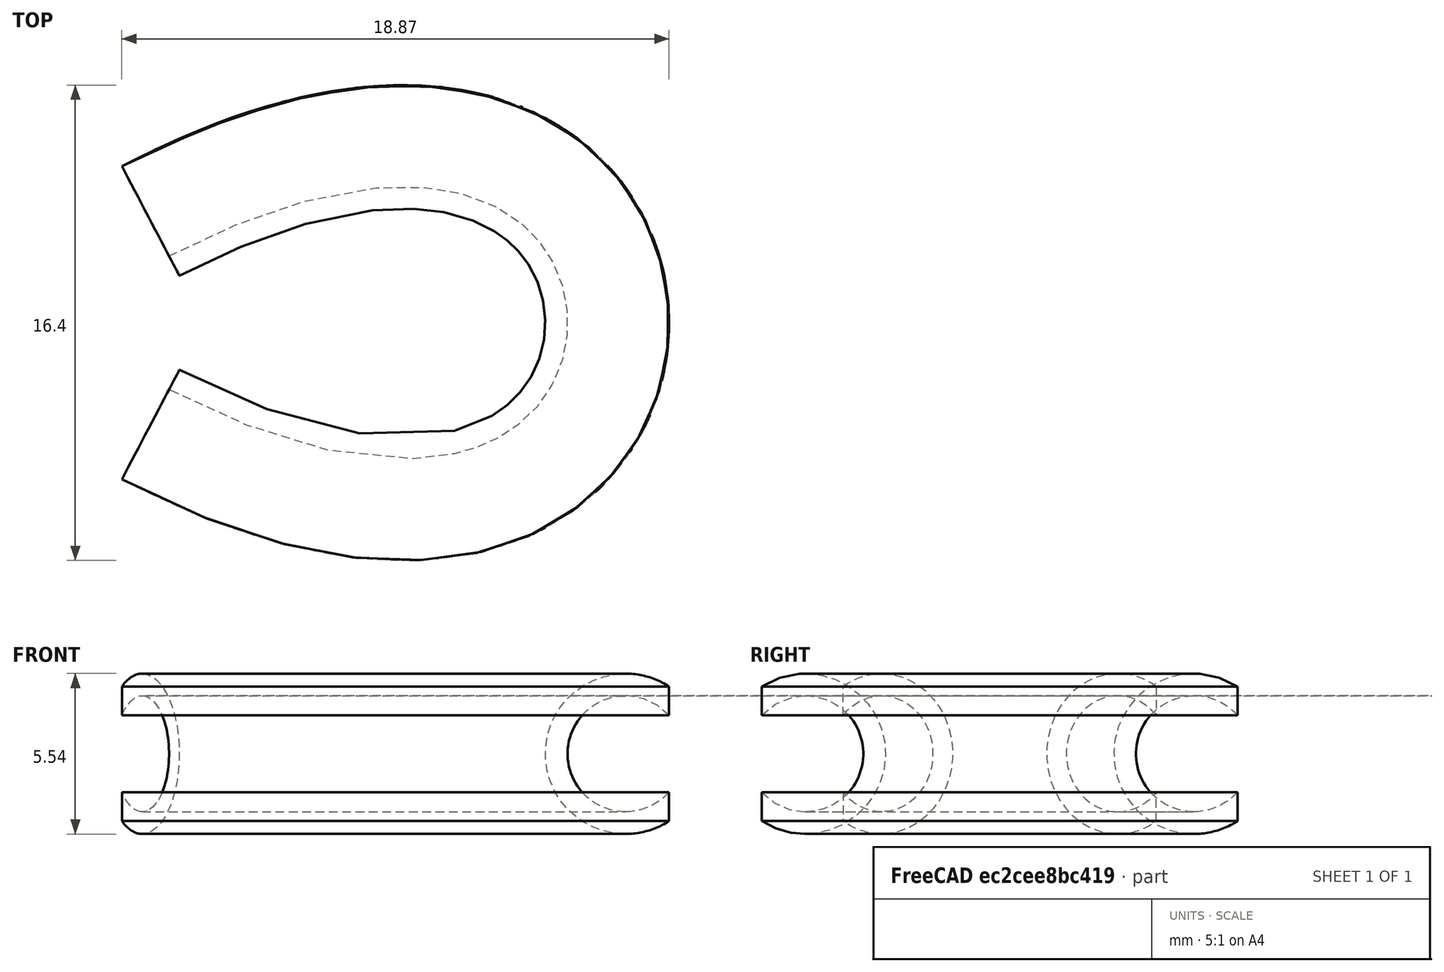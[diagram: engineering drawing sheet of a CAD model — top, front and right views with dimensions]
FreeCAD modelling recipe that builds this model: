
FCSTD DOCUMENT  (FreeCAD 0.20R24612 (Git))
Label: wire thimble
License: All rights reserved
LicenseURL: http://en.wikipedia.org/wiki/All_rights_reserved
objects: Sketcher::SketchObject×2, PartDesign::AdditivePipe×1, PartDesign::Body×1
note: 5 computed .brp shape members not serialized (recipe doc carries the construction recipe); baked Part::Feature solids carry a one-line shape summary decoded from their .brp

FEATURE [Sketcher::SketchObject] Sketch
  FullyConstrained = true
  MapMode = 5
  Placement = pos=(0,0,0) rot=(1,0,0;1.5708rad)
  Support = -> [XZ_Plane]
  sketch-geometry (4):
    g0: ArcOfCircle CenterX=0 CenterY=0 CenterZ=0 NormalX=0 NormalY=0 NormalZ=1 AngleXU=0 Radius=2.7651 StartAngle=0.997414 EndAngle=5.28577
    g1: ArcOfCircle CenterX=0 CenterY=0 CenterZ=0 NormalX=0 NormalY=0 NormalZ=1 AngleXU=0 Radius=2 StartAngle=0.722734 EndAngle=5.56045
    g2: LineSegment StartX=1.5 StartY=2.32288 StartZ=0 EndX=1.5 EndY=1.32288 EndZ=0
    g3: LineSegment StartX=1.5 StartY=-1.32288 StartZ=0 EndX=1.5 EndY=-2.32288 EndZ=0
  constraints (12):
    c: Radius(g1) = 2
    c: Coincident(g1,g-1)
    c: Coincident(g0,g1)
    c: Coincident(g2,g0)
    c: Coincident(g2,g1)
    c: Vertical(g2)
    c: Coincident(g3,g1)
    c: Coincident(g3,g0)
    c: Vertical(g3)
    c: Vertical(g1,g1)
    c: DistanceY(g2,g2) = 1
    c: DistanceX(g0,g1) = 1.5
FEATURE [Sketcher::SketchObject] Sketch001
  FullyConstrained = false
  MapMode = 5
  Support = -> [XY_Plane]
  sketch-geometry (7):
    g0-g3: Circle x4 (B-spline internal-alignment scaffolding for g4; pole/knot coordinates omitted)
    g4: BSplineCurve PolesCount=4 KnotsCount=2 Degree=3 IsPeriodic=0
    g5: GeomPoint X=-16.6579 Y=4.04883 Z=0
    g6: GeomPoint X=-16.6579 Y=-4.04883 Z=0
  constraints (9):
    c: Weight(g0) = 1
    c: Equal(g0,g1)
    c: Equal(g0,g2)
    c: Equal(g0,g3)
    c: InternalAlignment(g0-g3 -> g4) x4
    c: InternalAlignment(g5,g4)
    c: InternalAlignment(g6,g4)
    c: Symmetric(g1,g2,g-1)
    c: Symmetric(g4,g4,g-1)
FEATURE [PartDesign::AdditivePipe] AdditivePipe
  AuxilleryCurvelinear = true
  AuxillerySpineTangent = false
  Binormal = (0,0,0)
  Mode = 0
  Placement = pos=(0,0,0) rot=(1,0,0;1.5708rad)
  Profile = -> Sketch
  Refine = true
  Spine = -> Sketch001
  SpineTangent = false
  Transformation = 0
  Transition = 0
FEATURE [PartDesign::Body] Body
  Group = -> [Sketch,Sketch001,AdditivePipe]
  Origin = -> Origin
  Tip = -> AdditivePipe
